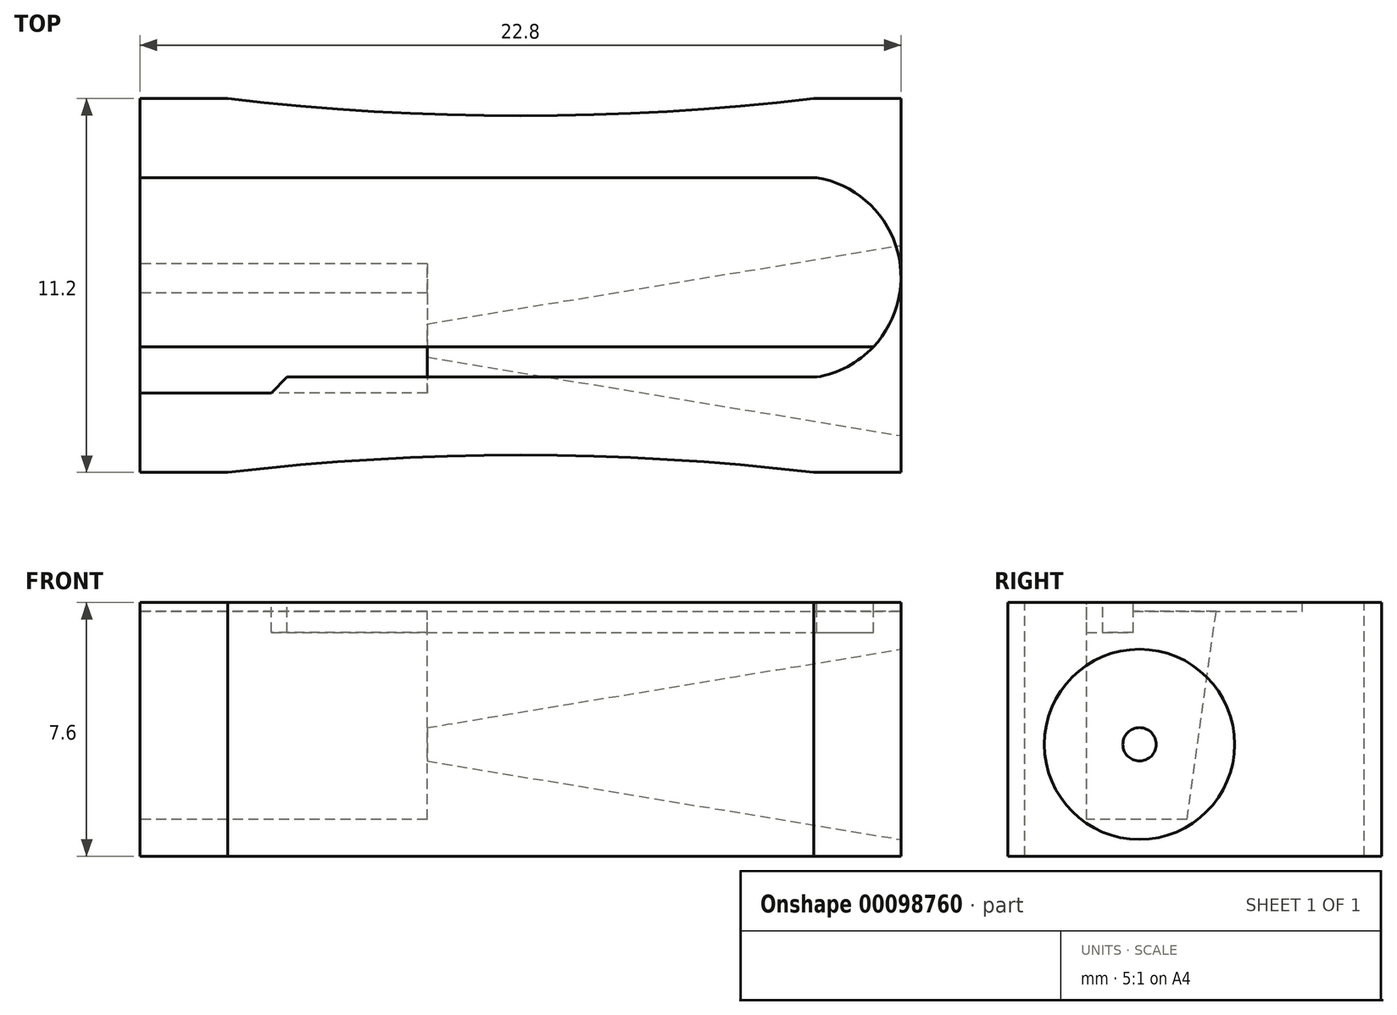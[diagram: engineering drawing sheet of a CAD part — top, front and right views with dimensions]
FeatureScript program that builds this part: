
annotation { "Feature Type Name" : "Feature", "Feature Type Description" : "" }
export const myFeature = defineFeature(function(context is Context, id is Id, definition is map)
    precondition{}
    {
        {
            var Q0;
            Q0=qCreatedBy(makeId("Front.planeOp"),FACE);
            var sketch = newSketch(context, id + "F0", { "sketchPlane" : qUnion([Q0])});
            skLineSegment(sketch, "E0", {"start": v(0, 0) * mm, "end": v(0, 7.6) * mm});
            skLineSegment(sketch, "E1", {"start": v(0, 7.6) * mm, "end": v(22.8, 7.6) * mm});
            skLineSegment(sketch, "E2", {"start": v(22.8, 7.6) * mm, "end": v(22.8, 0) * mm});
            skLineSegment(sketch, "E3", {"start": v(22.8, 0) * mm, "end": v(0, 0) * mm});
            skSolve(sketch);
        }
        {
            var Q0;
            Q0 = qSketchRegion(id + "F0", true);
            extrude(context, id + "F1", {"entities" : qUnion([Q0]), "depth" : 11.2 * mm});
        }
        {
            var Q0;
            Q0=makeQuery(id+"F1.opExtrude","SWEPT_FACE",FACE,{"disambiguationData":[OSD([sQuery(id+"F0.wireOp",EDGE,"E2")])]});
            var sketch = newSketch(context, id + "F2", { "sketchPlane" : qUnion([Q0])});
            skCircle(sketch, "E4", {"center": v(-7.25, 3.35) * mm, "radius": 2.85 * mm});
            skSolve(sketch);
        }
        {
            var Q0;
            Q0=makeQuery(id+"F1.opExtrude","CAP_FACE",FACE,{"disambiguationData":[OSD([sQuery(id+"F0.wireOp",EDGE,"E0"),sQuery(id+"F0.wireOp",EDGE,"E1"),sQuery(id+"F0.wireOp",EDGE,"E2"),sQuery(id+"F0.wireOp",EDGE,"E3")])],"isStart":false});
            cPlane(context, id + "F3", {"entities" : qUnion([Q0]), "cplaneType" : CPlaneType.OFFSET, "offset" : 3.95 * mm, "oppositeDirection" : true, "width" : 150 * mm, "height" : 150 * mm});
        }
        {
            var Q0;
            Q0=qCreatedBy(id+"F3.planeOp",FACE);
            var sketch = newSketch(context, id + "F4", { "sketchPlane" : qUnion([Q0])});
            skLineSegment(sketch, "E5", {"start": v(22.8, 0.5) * mm, "end": v(22.8, 3.35) * mm});
            skLineSegment(sketch, "E6", {"start": v(22.8, 3.35) * mm, "end": v(8.6, 3.35) * mm});
            skLineSegment(sketch, "E7", {"start": v(8.6, 3.35) * mm, "end": v(8.6, 2.85) * mm});
            skLineSegment(sketch, "E8", {"start": v(8.6, 2.85) * mm, "end": v(22.8, 0.5) * mm});
            skSolve(sketch);
        }
        {
            var Q0;
            Q0 = qSketchRegion(id + "F4", true);
            var Q1;
            Q1=sQuery(id+"F4.wireOp",EDGE,"E6");
            revolve(context, id + "F5", {"operationType" : NewBodyOperationType.REMOVE, "entities" : qUnion([Q0]), "axis" : qUnion([Q1]), "revolveType" : RevolveType.FULL, "oppositeDirection" : true});
        }
        {
            var Q0;
            Q0=makeQuery(id+"F1.opExtrude","SWEPT_FACE",FACE,{"disambiguationData":[OSD([sQuery(id+"F0.wireOp",EDGE,"E1")])]});
            var sketch = newSketch(context, id + "F6", { "sketchPlane" : qUnion([Q0])});
            skLineSegment(sketch, "E9", {"start": v(0, -2.37) * mm, "end": v(20.28, -2.37) * mm});
            skLineSegment(sketch, "E10", {"start": v(0, -2.37) * mm, "end": v(0, -7.44) * mm});
            skLineSegment(sketch, "E11", {"start": v(0, -8.83) * mm, "end": v(3.93, -8.83) * mm});
            skLineSegment(sketch, "E12", {"start": v(3.93, -8.83) * mm, "end": v(4.4, -8.35) * mm});
            skLineSegment(sketch, "E13", {"start": v(4.4, -8.35) * mm, "end": v(20.28, -8.35) * mm});
            skArc(sketch, "E14", {"start": v(20.28, -8.35) * mm, "mid": v(22.8, -5.36) * mm, "end": v(20.28, -2.37) * mm});
            skLineSegment(sketch, "E15", {"start": v(0, -7.44) * mm, "end": v(21.97, -7.44) * mm});
            skLineSegment(sketch, "E16", {"start": v(0, -7.44) * mm, "end": v(0, -8.83) * mm});
            skLineSegment(sketch, "E17", {"start": v(22.8, -11.2) * mm, "end": v(20.18, -11.2) * mm});
            skLineSegment(sketch, "E18", {"start": v(0, -11.2) * mm, "end": v(2.62, -11.2) * mm});
            skArc(sketch, "E19", {"start": v(20.18, -11.2) * mm, "mid": v(11.4, -10.68) * mm, "end": v(2.62, -11.2) * mm});
            skLineSegment(sketch, "E20", {"start": v(2.62, -11.2) * mm, "end": v(20.18, -11.2) * mm});
            skPoint(sketch, "E21.endSnap0", {"position": v(11.4, 0) * mm});
            skLineSegment(sketch, "E22", {"start": v(2.62, 0) * mm, "end": v(20.18, 0) * mm});
            skArc(sketch, "E23", {"start": v(2.62, 0) * mm, "mid": v(11.4, -0.52) * mm, "end": v(20.18, 0) * mm});
            skSolve(sketch);
        }
        {
            var Q0;
            Q0=makeQuery(id+"F6.imprint","IMPRINT",FACE,{"disambiguationData":[TD([[makeQuery(id+"F6.imprint","IMPRINT",EDGE,{"derivedFrom":sQuery(id+"F6.wireOp",EDGE,"E11")}),1.0]])]});
            extrude(context, id + "F7", {"entities" : qUnion([Q0]), "operationType" : NewBodyOperationType.REMOVE, "oppositeDirection" : true, "depth" : 0.9 * mm});
        }
        {
            var Q0;
            Q0=makeQuery(id+"F1.opExtrude","SWEPT_FACE",FACE,{"disambiguationData":[OSD([sQuery(id+"F0.wireOp",EDGE,"E0")])]});
            var sketch = newSketch(context, id + "F8", { "sketchPlane" : qUnion([Q0])});
            skLineSegment(sketch, "E24", {"start": v(5.83, 1.1) * mm, "end": v(8.83, 1.1) * mm});
            skLineSegment(sketch, "E25", {"start": v(8.83, 1.1) * mm, "end": v(8.83, 7.6) * mm});
            skLineSegment(sketch, "E26", {"start": v(5.83, 1.1) * mm, "end": v(4.95, 7.33) * mm});
            skLineSegment(sketch, "E27", {"start": v(4.95, 7.33) * mm, "end": v(8.83, 7.33) * mm});
            skSolve(sketch);
        }
        {
            var Q0;
            {var subQ7=sQuery(id+"F8.wireOp",EDGE,"E24");Q0=makeQuery(id+"F8.imprint","IMPRINT",FACE,{"disambiguationData":[TD([[makeQuery(id+"F8.imprint","IMPRINT",EDGE,{"derivedFrom":subQ7}),1.0]])]});}
            extrude(context, id + "F9", {"entities" : qUnion([Q0]), "operationType" : NewBodyOperationType.REMOVE, "oppositeDirection" : true, "depth" : 8.6 * mm});
        }
        {
            var Q0;
            Q0=makeQuery(id+"F6.imprint","IMPRINT",FACE,{"disambiguationData":[TD([[makeQuery(id+"F6.imprint","IMPRINT",EDGE,{"derivedFrom":sQuery(id+"F6.wireOp",EDGE,"E19")}),1.0]])]});
            extrude(context, id + "F10", {"entities" : qUnion([Q0]), "operationType" : NewBodyOperationType.REMOVE, "oppositeDirection" : true, "depth" : 7.6 * mm});
        }
        {
            var Q0;
            Q0=makeQuery(id+"F6.imprint","IMPRINT",FACE,{"disambiguationData":[TD([[makeQuery(id+"F6.imprint","IMPRINT",EDGE,{"derivedFrom":sQuery(id+"F6.wireOp",EDGE,"E22")}),-1.0]])]});
            extrude(context, id + "F11", {"entities" : qUnion([Q0]), "operationType" : NewBodyOperationType.REMOVE, "oppositeDirection" : true, "depth" : 7.6 * mm});
        }
        {
            var Q0;
            {var subQ1=sQuery(id+"F6.wireOp",EDGE,"E9");Q0=makeQuery(id+"F6.imprint","IMPRINT",FACE,{"disambiguationData":[TD([[makeQuery(id+"F6.imprint","IMPRINT",EDGE,{"derivedFrom":subQ1}),-1.0]])]});}
            extrude(context, id + "F12", {"entities" : qUnion([Q0]), "oppositeDirection" : true, "depth" : 0.27 * mm});
        }
    });
